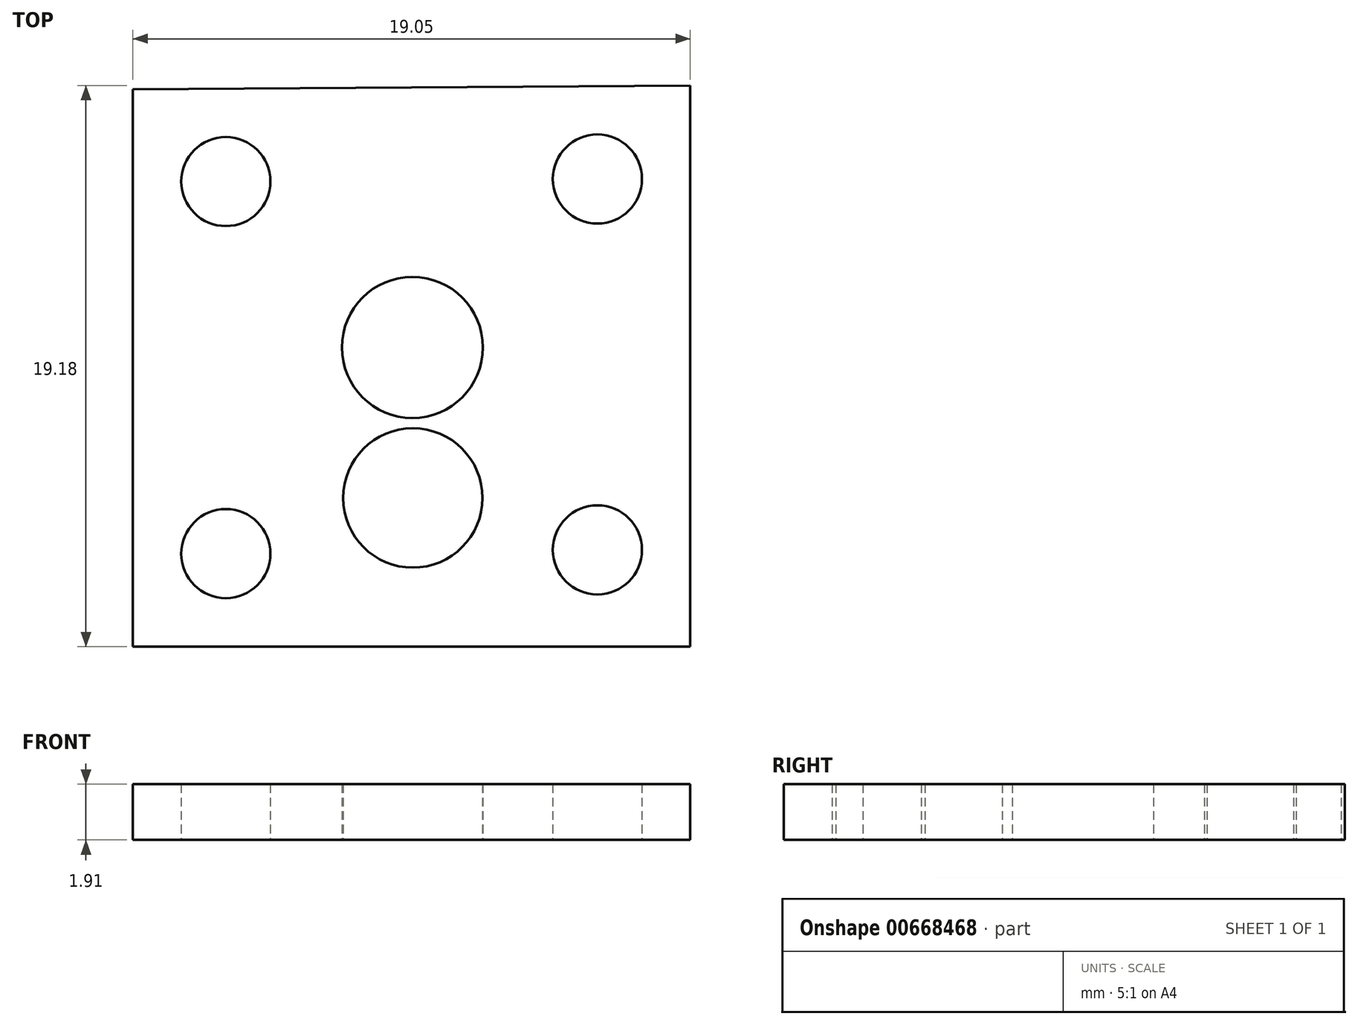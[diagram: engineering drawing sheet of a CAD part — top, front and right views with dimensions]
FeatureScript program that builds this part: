
annotation { "Feature Type Name" : "Feature", "Feature Type Description" : "" }
export const myFeature = defineFeature(function(context is Context, id is Id, definition is map)
    precondition{}
    {
        {
            var Q0;
            Q0=qCreatedBy(makeId("Top.planeOp"),FACE);
            var sketch = newSketch(context, id + "F0", { "sketchPlane" : qUnion([Q0])});
            skLineSegment(sketch, "E0.left", {"start": v(-21.5, 15.78) * mm, "end": v(-21.5, 14.26) * mm});
            skPoint(sketch, "E1", {"position": v(-5.63, 11.08) * mm});
            skPoint(sketch, "E2", {"position": v(-18.37, 10.57) * mm});
            skLineSegment(sketch, "E3.trimOffspring", {"start": v(-2.46, 15.9) * mm, "end": v(-2.46, 14.38) * mm});
            skCircle(sketch, "E4", {"center": v(-11.94, 16.16) * mm, "radius": 2.38 * mm});
            skLineSegment(sketch, "E5", {"start": v(-21.5, 14.26) * mm, "end": v(-21.5, 26.98) * mm});
            skLineSegment(sketch, "E6", {"start": v(-2.46, 15.9) * mm, "end": v(-2.46, 27.06) * mm});
            skLineSegment(sketch, "E7", {"start": v(-18.35, 30.15) * mm, "end": v(-5.65, 30.24) * mm});
            skPoint(sketch, "E8.visualSharp", {"position": v(-21.5, 30.13) * mm});
            skPoint(sketch, "E9.visualSharp", {"position": v(-2.46, 30.26) * mm});
            skPoint(sketch, "E10.orphan", {"position": v(-11.98, 30.2) * mm});
            skLineSegment(sketch, "E11", {"start": v(-18.33, 11.08) * mm, "end": v(-5.63, 11.08) * mm});
            skCircle(sketch, "E12", {"center": v(-11.96, 21.3) * mm, "radius": 2.4 * mm});
            skCircle(sketch, "E13", {"center": v(-18.33, 14.26) * mm, "radius": 1.52 * mm});
            skCircle(sketch, "E14", {"center": v(-18.33, 26.98) * mm, "radius": 1.52 * mm});
            skCircle(sketch, "E15", {"center": v(-5.63, 27.06) * mm, "radius": 1.52 * mm});
            skCircle(sketch, "E16", {"center": v(-5.63, 14.38) * mm, "radius": 1.52 * mm});
            skLineSegment(sketch, "E17", {"start": v(-2.46, 14.38) * mm, "end": v(-2.46, 14.26) * mm});
            skLineSegment(sketch, "E18", {"start": v(-5.63, 11.08) * mm, "end": v(-5.63, 11.08) * mm});
            skPoint(sketch, "E19.visualSharp", {"position": v(-2.46, 11.08) * mm});
            skLineSegment(sketch, "E20", {"start": v(-21.5, 14.26) * mm, "end": v(-21.5, 11.08) * mm});
            skLineSegment(sketch, "E21", {"start": v(-21.5, 11.08) * mm, "end": v(-18.33, 11.08) * mm});
            skLineSegment(sketch, "E22", {"start": v(-5.63, 11.08) * mm, "end": v(-2.46, 11.08) * mm});
            skLineSegment(sketch, "E23", {"start": v(-2.46, 14.26) * mm, "end": v(-2.46, 11.08) * mm});
            skLineSegment(sketch, "E24", {"start": v(-2.46, 27.06) * mm, "end": v(-2.46, 30.26) * mm});
            skLineSegment(sketch, "E25", {"start": v(-5.65, 30.24) * mm, "end": v(-2.46, 30.26) * mm});
            skLineSegment(sketch, "E26", {"start": v(-21.5, 26.98) * mm, "end": v(-21.5, 30.13) * mm});
            skLineSegment(sketch, "E27", {"start": v(-18.35, 30.15) * mm, "end": v(-21.5, 30.13) * mm});
            skSolve(sketch);
        }
        {
            var Q0;
            Q0=makeQuery(id+"F0.imprint","IMPRINT",FACE,{"disambiguationData":[TD([[makeQuery(id+"F0.imprint","IMPRINT",EDGE,{"derivedFrom":sQuery(id+"F0.wireOp",EDGE,"E3.trimOffspring")}),-1.0]])]});
            extrude(context, id + "F1", {"entities" : qUnion([Q0]), "depth" : 1.9 * mm});
        }
    });
